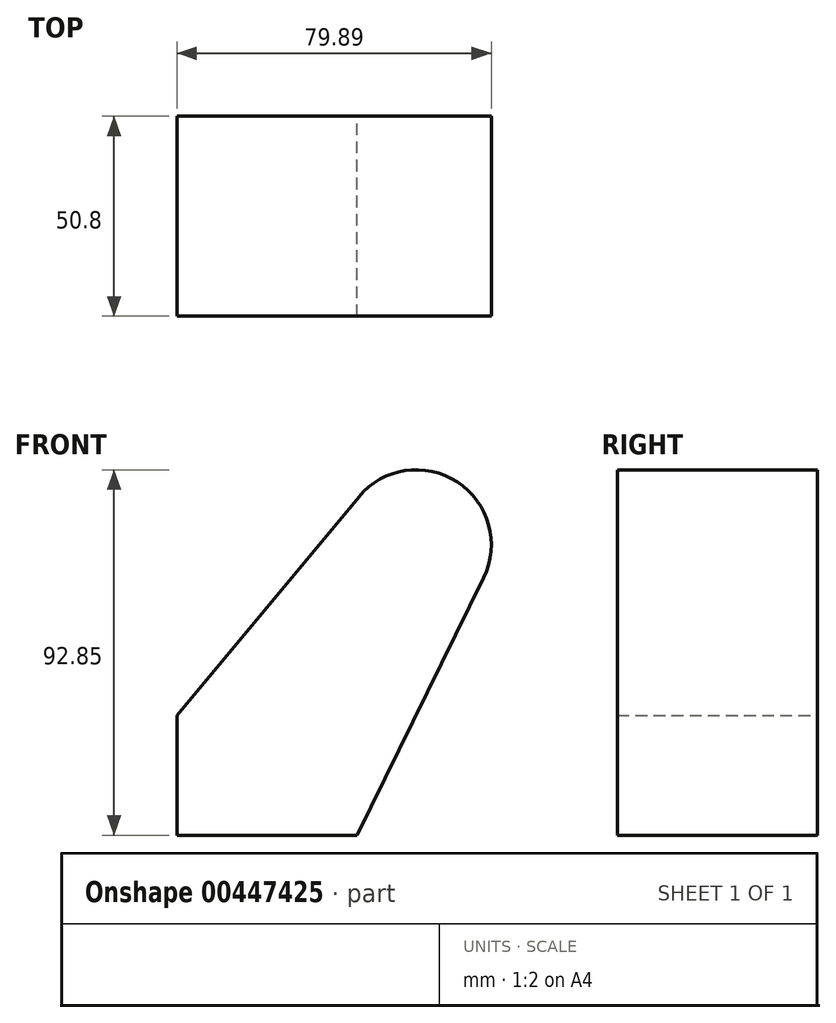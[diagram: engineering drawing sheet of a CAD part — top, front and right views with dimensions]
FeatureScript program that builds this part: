
annotation { "Feature Type Name" : "Feature", "Feature Type Description" : "" }
export const myFeature = defineFeature(function(context is Context, id is Id, definition is map)
    precondition{}
    {
        {
            var Q0;
            Q0=qCreatedBy(makeId("Front.planeOp"),FACE);
            var sketch = newSketch(context, id + "F0", { "sketchPlane" : qUnion([Q0])});
            skLineSegment(sketch, "E0.bottom", {"start": v(-15.16, 11.2) * mm, "end": v(30.56, 11.2) * mm});
            skLineSegment(sketch, "E0.top", {"start": v(-15.16, -19.28) * mm, "end": v(30.56, -19.28) * mm});
            skLineSegment(sketch, "E0.left", {"start": v(-15.16, 11.2) * mm, "end": v(-15.16, -19.28) * mm});
            skLineSegment(sketch, "E0.right", {"start": v(30.56, 11.2) * mm, "end": v(30.56, -19.28) * mm});
            skCircle(sketch, "E1", {"center": v(45.68, 54.52) * mm, "radius": 19.05 * mm});
            skLineSegment(sketch, "E2", {"start": v(30.56, -19.28) * mm, "end": v(62.77, 46.1) * mm});
            skLineSegment(sketch, "E3", {"start": v(-15.16, 11.2) * mm, "end": v(31.04, 66.7) * mm});
            skSolve(sketch);
        }
        {
            var Q0;
            Q0 = qSketchRegion(id + "F0", true);
            extrude(context, id + "F1", {"entities" : qUnion([Q0]), "endBound" : BoundingType.SYMMETRIC, "depth" : 50.8 * mm});
        }
    });
